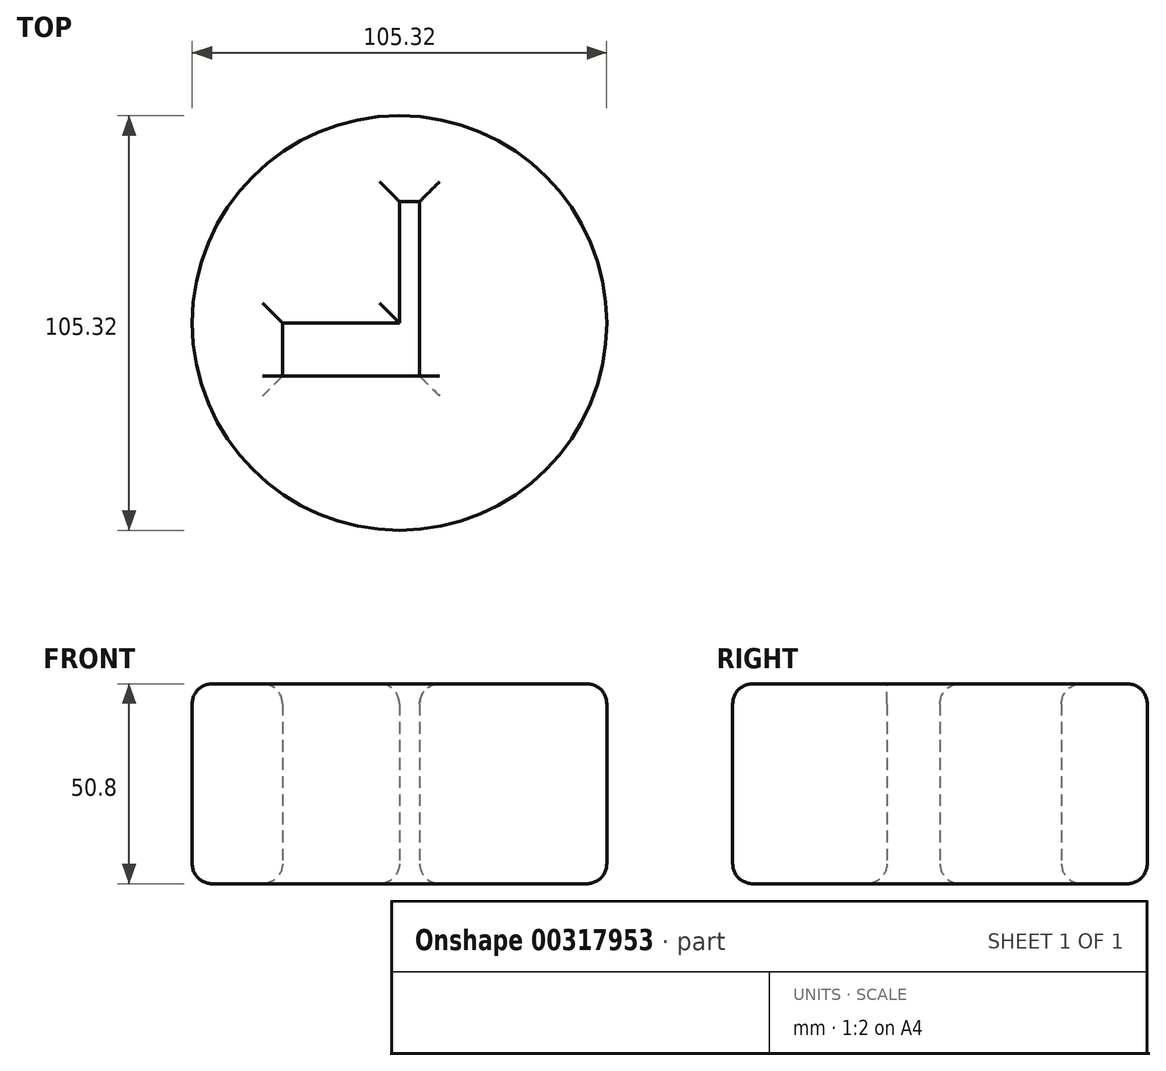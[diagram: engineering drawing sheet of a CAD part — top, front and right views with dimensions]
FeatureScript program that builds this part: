
annotation { "Feature Type Name" : "Feature", "Feature Type Description" : "" }
export const myFeature = defineFeature(function(context is Context, id is Id, definition is map)
    precondition{}
    {
        {
            var Q0;
            Q0=qCreatedBy(makeId("Top.planeOp"),FACE);
            var sketch = newSketch(context, id + "F0", { "sketchPlane" : qUnion([Q0])});
            skCircle(sketch, "E0", {"center": v(0, 0) * mm, "radius": 52.66 * mm});
            skLineSegment(sketch, "E1.bottom", {"start": v(5.15, -13.48) * mm, "end": v(-29.71, -13.48) * mm});
            skLineSegment(sketch, "E1.top", {"start": v(5.15, 0) * mm, "end": v(-29.71, 0) * mm});
            skLineSegment(sketch, "E1.left", {"start": v(5.15, -13.48) * mm, "end": v(5.15, 0) * mm});
            skLineSegment(sketch, "E1.right", {"start": v(-29.71, -13.48) * mm, "end": v(-29.71, 0) * mm});
            skLineSegment(sketch, "E2.bottom", {"start": v(5.15, 0) * mm, "end": v(0, 0) * mm});
            skLineSegment(sketch, "E2.top", {"start": v(5.15, 30.87) * mm, "end": v(0, 30.87) * mm});
            skLineSegment(sketch, "E2.left", {"start": v(5.15, 0) * mm, "end": v(5.15, 30.87) * mm});
            skLineSegment(sketch, "E2.right", {"start": v(0, 0) * mm, "end": v(0, 30.87) * mm});
            skSolve(sketch);
        }
        {
            var Q0;
            Q0=makeQuery(id+"F0.imprint","IMPRINT",FACE,{"disambiguationData":[TD([[makeQuery(id+"F0.imprint","IMPRINT",EDGE,{"derivedFrom":sQuery(id+"F0.wireOp",EDGE,"E0")}),1.0]])]});
            extrude(context, id + "F1", {"entities" : qUnion([Q0]), "depth" : 50.8 * mm});
        }
        {
            var Q0;
            Q0=makeQuery(id+"F1.opExtrude","CAP_EDGE",EDGE,{"disambiguationData":[OSD([sQuery(id+"F0.wireOp",EDGE,"E0")])],"isStart":false});
            var Q1;
            Q1=makeQuery(id+"F1.opExtrude","CAP_EDGE",EDGE,{"disambiguationData":[OSD([sQuery(id+"F0.wireOp",EDGE,"E1.top")])],"isStart":false});
            var Q2;
            Q2=makeQuery(id+"F1.opExtrude","CAP_EDGE",EDGE,{"disambiguationData":[OSD([sQuery(id+"F0.wireOp",EDGE,"E1.right")])],"isStart":false});
            var Q3;
            Q3=makeQuery(id+"F1.opExtrude","CAP_EDGE",EDGE,{"disambiguationData":[OSD([sQuery(id+"F0.wireOp",EDGE,"E1.left"),sQuery(id+"F0.wireOp",EDGE,"E2.left")])],"isStart":false});
            var Q4;
            Q4=makeQuery(id+"F1.opExtrude","CAP_EDGE",EDGE,{"disambiguationData":[OSD([sQuery(id+"F0.wireOp",EDGE,"E2.right")])],"isStart":false});
            var Q5;
            Q5=makeQuery(id+"F1.opExtrude","CAP_EDGE",EDGE,{"disambiguationData":[OSD([sQuery(id+"F0.wireOp",EDGE,"E2.top")])],"isStart":false});
            var Q6;
            Q6=makeQuery(id+"F1.opExtrude","CAP_EDGE",EDGE,{"disambiguationData":[OSD([sQuery(id+"F0.wireOp",EDGE,"E0")])],"isStart":true});
            var Q7;
            Q7=makeQuery(id+"F1.opExtrude","CAP_FACE",FACE,{"disambiguationData":[OSD([sQuery(id+"F0.wireOp",EDGE,"E0"),sQuery(id+"F0.wireOp",EDGE,"E1.bottom"),sQuery(id+"F0.wireOp",EDGE,"E1.top"),sQuery(id+"F0.wireOp",EDGE,"E1.left"),sQuery(id+"F0.wireOp",EDGE,"E1.right"),sQuery(id+"F0.wireOp",EDGE,"E2.top"),sQuery(id+"F0.wireOp",EDGE,"E2.left"),sQuery(id+"F0.wireOp",EDGE,"E2.right")])],"isStart":true});
            fillet(context, id + "F2", {"entities" : qUnion([Q0, Q1, Q2, Q3, Q4, Q5, Q6, Q7]), "radius" : 5.08 * mm, "tangentPropagation" : true, "allowEdgeOverflow" : false});
        }
    });
